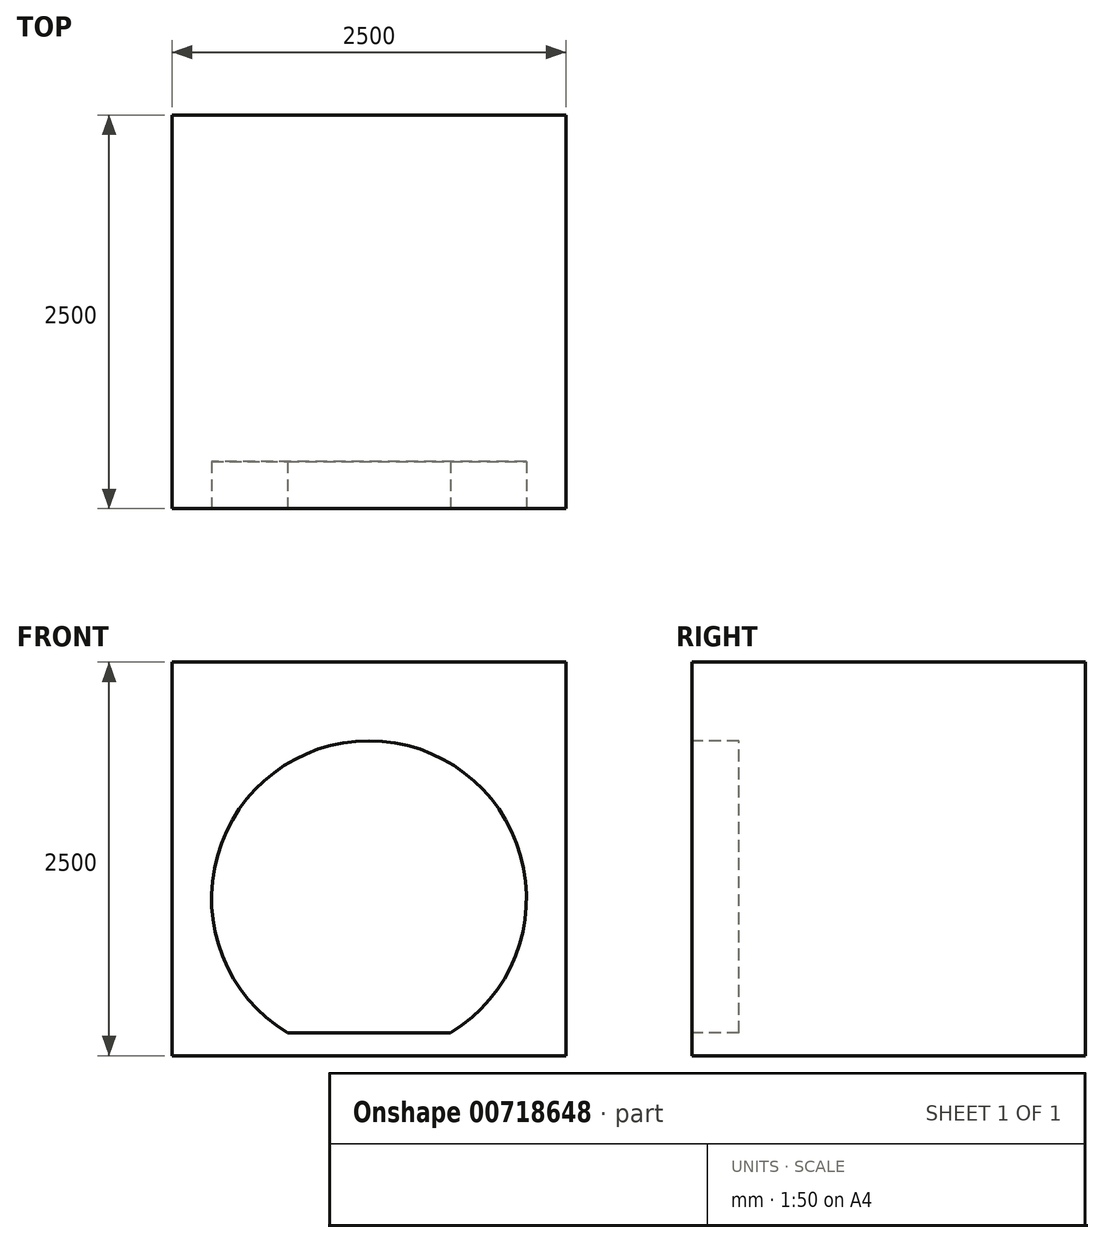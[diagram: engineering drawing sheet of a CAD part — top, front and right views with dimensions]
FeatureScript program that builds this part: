
annotation { "Feature Type Name" : "Feature", "Feature Type Description" : "" }
export const myFeature = defineFeature(function(context is Context, id is Id, definition is map)
    precondition{}
    {
        {
            var Q0;
            Q0=qCreatedBy(makeId("Top.planeOp"),FACE);
            var sketch = newSketch(context, id + "F0", { "sketchPlane" : qUnion([Q0])});
            skLineSegment(sketch, "E0.bottom", {"start": v(0, 0) * mm, "end": v(2500, 0) * mm});
            skLineSegment(sketch, "E0.top", {"start": v(0, 2500) * mm, "end": v(2500, 2500) * mm});
            skLineSegment(sketch, "E0.left", {"start": v(0, 0) * mm, "end": v(0, 2500) * mm});
            skLineSegment(sketch, "E0.right", {"start": v(2500, 0) * mm, "end": v(2500, 2500) * mm});
            skSolve(sketch);
        }
        {
            var Q0;
            Q0=makeQuery(id+"F0.imprint","IMPRINT",FACE,{"disambiguationData":[TD([[makeQuery(id+"F0.imprint","IMPRINT",EDGE,{"derivedFrom":sQuery(id+"F0.wireOp",EDGE,"E0.bottom")}),1.0]])]});
            extrude(context, id + "F1", {"entities" : qUnion([Q0]), "depth" : 2500 * mm, "offsetDistance" : 25 * mm});
        }
        {
            var Q0;
            Q0=makeQuery(id+"F1.opExtrude","SWEPT_FACE",FACE,{"disambiguationData":[OSD([sQuery(id+"F0.wireOp",EDGE,"E0.bottom")])]});
            var sketch = newSketch(context, id + "F2", { "sketchPlane" : qUnion([Q0])});
            skLineSegment(sketch, "E1", {"start": v(1250, 2500) * mm, "end": v(1250, 0) * mm, "construction": true});
            skCircle(sketch, "E2", {"center": v(1250, 1000) * mm, "radius": 1000 * mm});
            skLineSegment(sketch, "E3", {"start": v(731.37, 145) * mm, "end": v(1768.63, 145) * mm});
            skSolve(sketch);
        }
        {
            var Q0;
            {var subQ0=sQuery(id+"F2.wireOp",EDGE,"E3");Q0=makeQuery(id+"F2.imprint","IMPRINT",FACE,{"disambiguationData":[TD([[makeQuery(id+"F2.imprint","IMPRINT",EDGE,{"derivedFrom":subQ0}),1.0]])]});}
            extrude(context, id + "F3", {"entities" : qUnion([Q0]), "operationType" : NewBodyOperationType.REMOVE, "oppositeDirection" : true, "depth" : 300 * mm, "offsetDistance" : 25 * mm});
        }
    });
